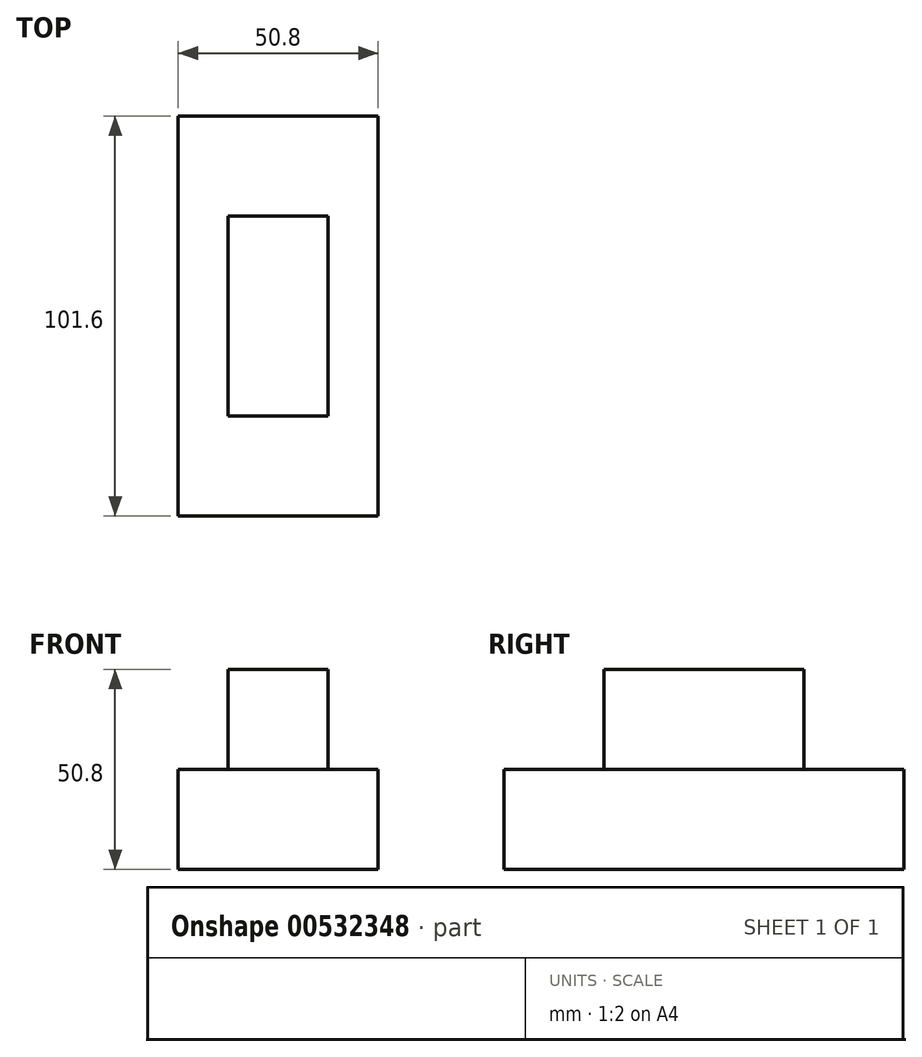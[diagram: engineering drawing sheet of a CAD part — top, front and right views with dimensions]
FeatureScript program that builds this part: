
annotation { "Feature Type Name" : "Feature", "Feature Type Description" : "" }
export const myFeature = defineFeature(function(context is Context, id is Id, definition is map)
    precondition{}
    {
        {
            var Q0;
            Q0=qCreatedBy(makeId("Top.planeOp"),FACE);
            var sketch = newSketch(context, id + "F0", { "sketchPlane" : qUnion([Q0])});
            skLineSegment(sketch, "E0.bottom", {"start": v(-25.4, 50.8) * mm, "end": v(25.4, 50.8) * mm});
            skLineSegment(sketch, "E0.top", {"start": v(-25.4, -50.8) * mm, "end": v(25.4, -50.8) * mm});
            skLineSegment(sketch, "E0.left", {"start": v(-25.4, 50.8) * mm, "end": v(-25.4, -50.8) * mm});
            skLineSegment(sketch, "E0.right", {"start": v(25.4, 50.8) * mm, "end": v(25.4, -50.8) * mm});
            skPoint(sketch, "E0.middle", {"position": v(0, 0) * mm});
            skSolve(sketch);
        }
        {
            var Q0;
            Q0=makeQuery(id+"F0.imprint","IMPRINT",FACE,{"disambiguationData":[TD([[makeQuery(id+"F0.imprint","IMPRINT",EDGE,{"derivedFrom":sQuery(id+"F0.wireOp",EDGE,"E0.bottom")}),-1.0]])]});
            extrude(context, id + "F1", {"entities" : qUnion([Q0]), "depth" : 25.4 * mm, "offsetDistance" : 25.4 * mm});
        }
        {
            var Q0;
            Q0=makeQuery(id+"F1.opExtrude","CAP_FACE",FACE,{"disambiguationData":[OSD([sQuery(id+"F0.wireOp",EDGE,"E0.bottom"),sQuery(id+"F0.wireOp",EDGE,"E0.top"),sQuery(id+"F0.wireOp",EDGE,"E0.left"),sQuery(id+"F0.wireOp",EDGE,"E0.right")])],"isStart":false});
            var sketch = newSketch(context, id + "F2", { "sketchPlane" : qUnion([Q0])});
            skLineSegment(sketch, "E1.bottom", {"start": v(-12.7, 25.4) * mm, "end": v(12.7, 25.4) * mm});
            skLineSegment(sketch, "E1.top", {"start": v(-12.7, -25.4) * mm, "end": v(12.7, -25.4) * mm});
            skLineSegment(sketch, "E1.left", {"start": v(-12.7, 25.4) * mm, "end": v(-12.7, -25.4) * mm});
            skLineSegment(sketch, "E1.right", {"start": v(12.7, 25.4) * mm, "end": v(12.7, -25.4) * mm});
            skPoint(sketch, "E1.middle", {"position": v(0, 0) * mm});
            skSolve(sketch);
        }
        {
            var Q0;
            Q0=makeQuery(id+"F2.imprint","IMPRINT",FACE,{"disambiguationData":[TD([[makeQuery(id+"F2.imprint","IMPRINT",EDGE,{"derivedFrom":sQuery(id+"F2.wireOp",EDGE,"E1.bottom")}),-1.0]])]});
            extrude(context, id + "F3", {"entities" : qUnion([Q0]), "operationType" : NewBodyOperationType.ADD, "depth" : 25.4 * mm, "offsetDistance" : 25.4 * mm});
        }
    });
